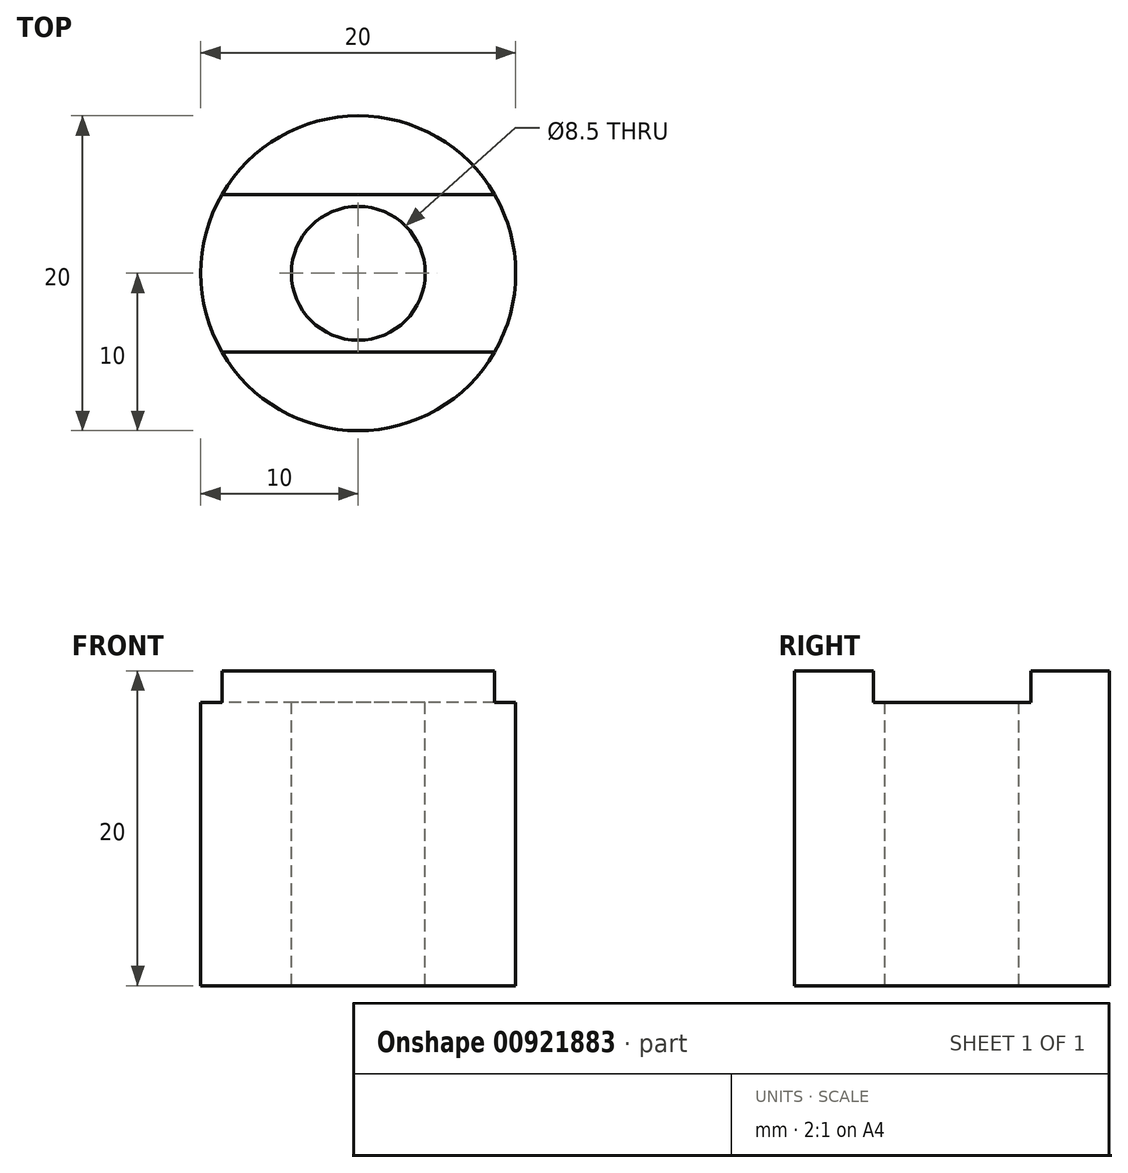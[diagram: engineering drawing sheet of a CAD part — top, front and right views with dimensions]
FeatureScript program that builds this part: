
annotation { "Feature Type Name" : "Feature", "Feature Type Description" : "" }
export const myFeature = defineFeature(function(context is Context, id is Id, definition is map)
    precondition{}
    {
        {
            var Q0;
            Q0=qCreatedBy(makeId("Top.planeOp"),FACE);
            var sketch = newSketch(context, id + "F0", { "sketchPlane" : qUnion([Q0])});
            skCircle(sketch, "E0", {"center": v(0, 0) * mm, "radius": 10 * mm});
            skSolve(sketch);
        }
        {
            var Q0;
            Q0 = qSketchRegion(id + "F0", true);
            extrude(context, id + "F1", {"entities" : qUnion([Q0]), "oppositeDirection" : true, "depth" : 20 * mm, "offsetDistance" : 25 * mm});
        }
        {
            var Q0;
            Q0=qCreatedBy(makeId("Top.planeOp"),FACE);
            var sketch = newSketch(context, id + "F2", { "sketchPlane" : qUnion([Q0])});
            skCircle(sketch, "E1", {"center": v(0, 0) * mm, "radius": 4.25 * mm});
            skSolve(sketch);
        }
        {
            var Q0;
            Q0 = qSketchRegion(id + "F2", true);
            extrude(context, id + "F3", {"entities" : qUnion([Q0]), "operationType" : NewBodyOperationType.REMOVE, "endBound" : BoundingType.THROUGH_ALL, "oppositeDirection" : true, "depth" : 25 * mm, "offsetDistance" : 25 * mm});
        }
        {
            var Q0;
            Q0=makeQuery(id+"F1.opExtrude","CAP_FACE",FACE,{"disambiguationData":[OSD([sQuery(id+"F0.wireOp",EDGE,"E0")])],"isStart":true});
            var sketch = newSketch(context, id + "F4", { "sketchPlane" : qUnion([Q0])});
            skLineSegment(sketch, "E2.bottom", {"start": v(11.57, -5) * mm, "end": v(-11.57, -5) * mm});
            skLineSegment(sketch, "E2.top", {"start": v(11.57, 5) * mm, "end": v(-11.57, 5) * mm});
            skLineSegment(sketch, "E2.left", {"start": v(11.57, -5) * mm, "end": v(11.57, 5) * mm});
            skLineSegment(sketch, "E2.right", {"start": v(-11.57, -5) * mm, "end": v(-11.57, 5) * mm});
            skPoint(sketch, "E2.middle", {"position": v(0, 0) * mm});
            skSolve(sketch);
        }
        {
            var Q0;
            Q0 = qSketchRegion(id + "F4", true);
            extrude(context, id + "F5", {"entities" : qUnion([Q0]), "operationType" : NewBodyOperationType.REMOVE, "oppositeDirection" : true, "depth" : 2 * mm, "offsetDistance" : 25 * mm});
        }
    });
